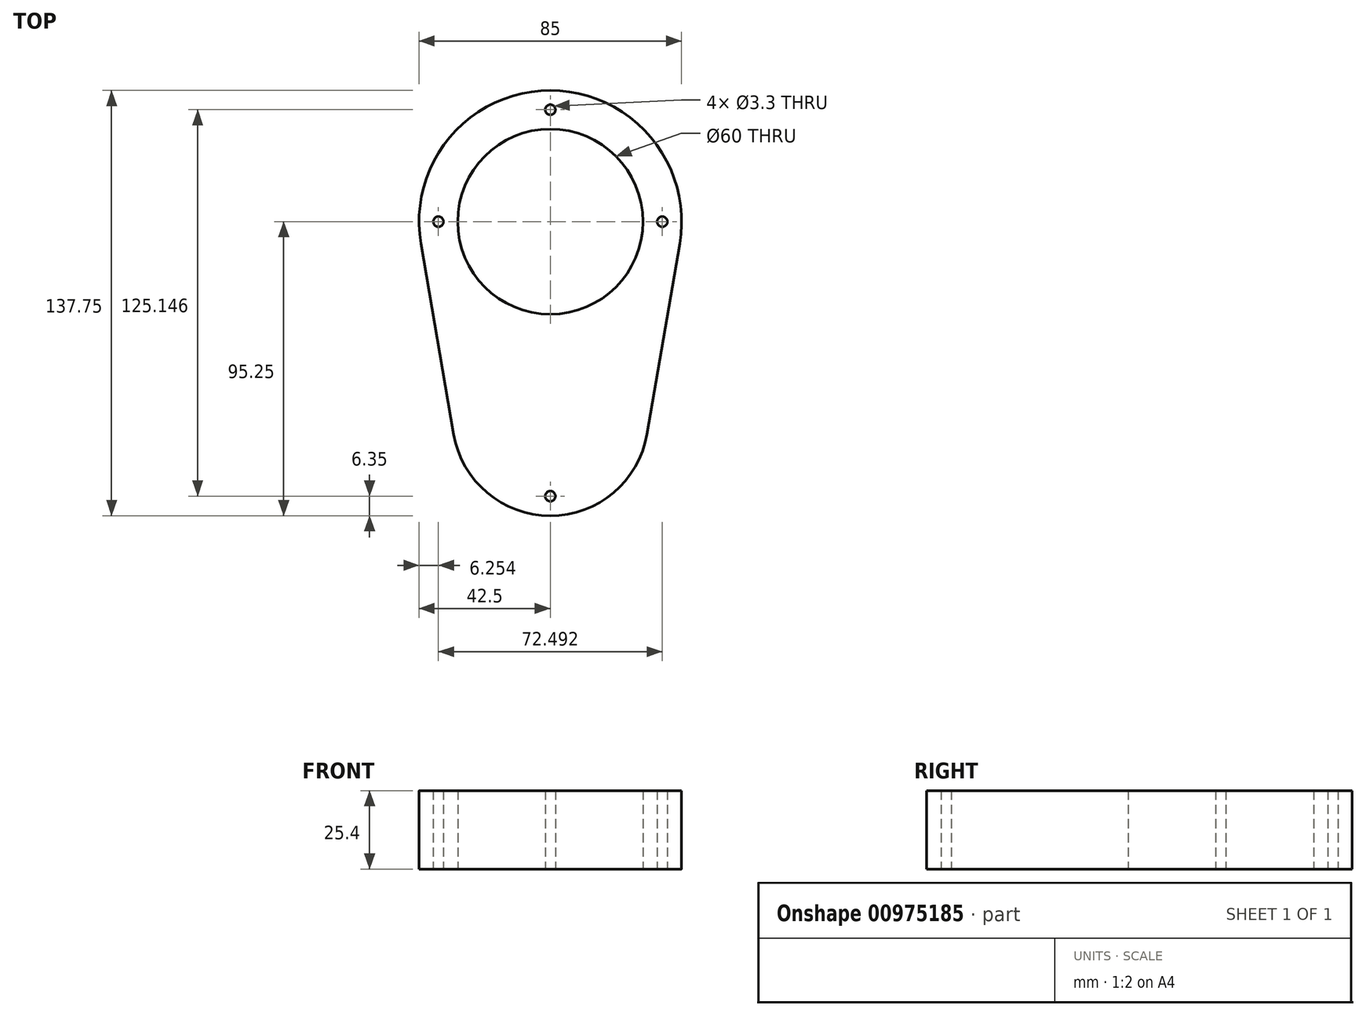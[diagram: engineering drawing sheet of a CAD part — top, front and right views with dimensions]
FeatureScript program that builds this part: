
annotation { "Feature Type Name" : "Feature", "Feature Type Description" : "" }
export const myFeature = defineFeature(function(context is Context, id is Id, definition is map)
    precondition{}
    {
        {
            var Q0;
            Q0=qCreatedBy(makeId("Top.planeOp"),FACE);
            var sketch = newSketch(context, id + "F0", { "sketchPlane" : qUnion([Q0])});
            skCircle(sketch, "E0", {"center": v(0, 0) * mm, "radius": 30 * mm});
            skLineSegment(sketch, "E1", {"start": v(-41.89, -7.2) * mm, "end": v(-41.89, -7.2) * mm});
            skLineSegment(sketch, "E2", {"start": v(31.3, -68.88) * mm, "end": v(41.89, -7.2) * mm});
            skLineSegment(sketch, "E3", {"start": v(-41.89, -7.2) * mm, "end": v(-31.3, -68.88) * mm});
            skArc(sketch, "E4", {"start": v(41.89, -7.2) * mm, "mid": v(0, 42.5) * mm, "end": v(-41.89, -7.2) * mm});
            skArc(sketch, "E5", {"start": v(-41.89, -7.2) * mm, "mid": v(0, -42.5) * mm, "end": v(41.89, -7.2) * mm, "construction": true});
            skArc(sketch, "E6", {"start": v(31.3, -68.88) * mm, "mid": v(0, -31.75) * mm, "end": v(-31.3, -68.87) * mm, "construction": true});
            skArc(sketch, "E7", {"start": v(-31.3, -68.88) * mm, "mid": v(0, -95.25) * mm, "end": v(31.3, -68.88) * mm});
            skCircle(sketch, "E8", {"center": v(0, 0) * mm, "radius": 36.25 * mm, "construction": true});
            skCircle(sketch, "E9", {"center": v(0, 36.25) * mm, "radius": 1.65 * mm});
            skCircle(sketch, "E10", {"center": v(0, -88.9) * mm, "radius": 1.65 * mm});
            skCircle(sketch, "E11.1.0", {"center": v(-36.25, 0) * mm, "radius": 1.65 * mm});
            skCircle(sketch, "E11.3.0", {"center": v(36.25, 0) * mm, "radius": 1.65 * mm});
            skSolve(sketch);
        }
        {
            var Q0;
            Q0=qSketchRegion(id+"F0",true);
            extrude(context, id + "F1", {"entities" : qUnion([Q0]), "depth" : 25.4 * mm, "offsetDistance" : 25.4 * mm});
        }
    });
